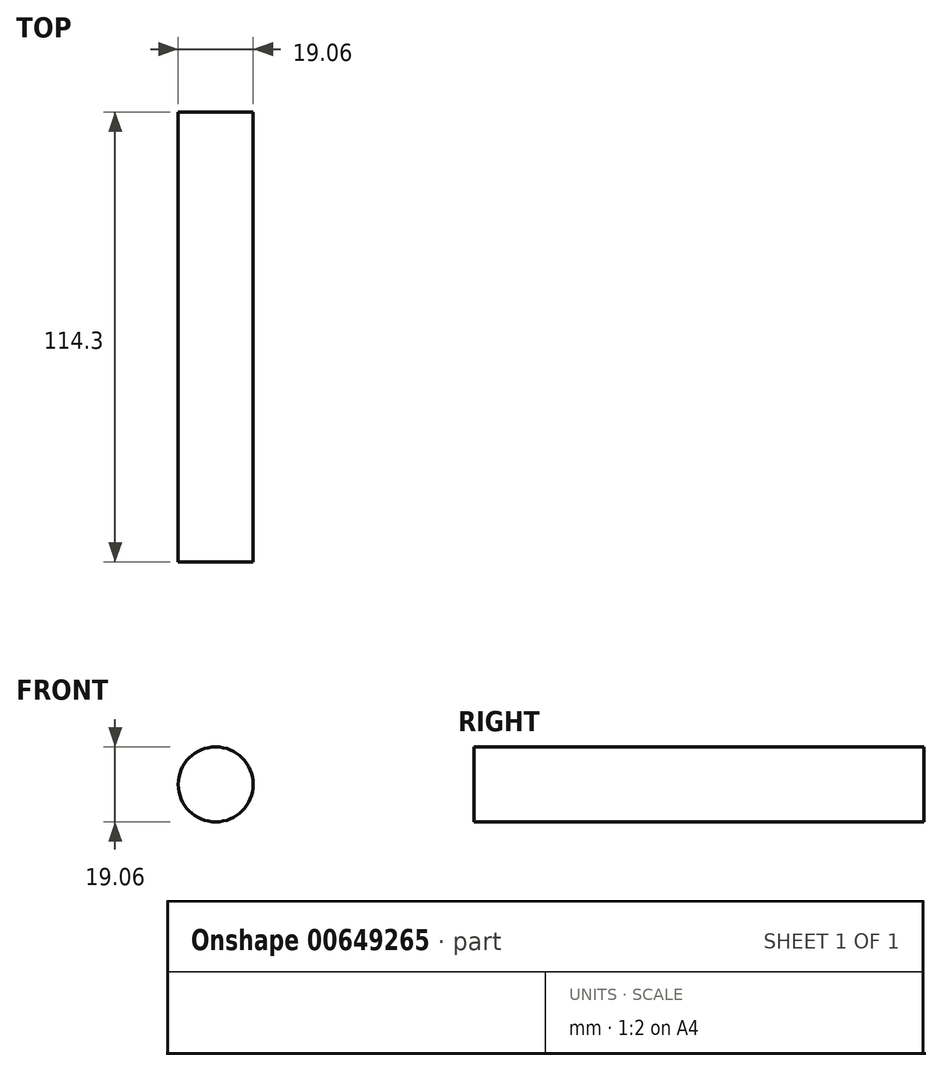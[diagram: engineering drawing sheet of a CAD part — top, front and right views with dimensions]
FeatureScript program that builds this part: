
annotation { "Feature Type Name" : "Feature", "Feature Type Description" : "" }
export const myFeature = defineFeature(function(context is Context, id is Id, definition is map)
    precondition{}
    {
        {
            var Q0;
            Q0=qCreatedBy(makeId("Front.planeOp"),FACE);
            var sketch = newSketch(context, id + "F0", { "sketchPlane" : qUnion([Q0])});
            skCircle(sketch, "E0", {"center": v(0, 0) * mm, "radius": 9.53 * mm});
            skSolve(sketch);
        }
        {
            var Q0;
            Q0=makeQuery(id+"F0.imprint","IMPRINT",FACE,{"disambiguationData":[TD([[makeQuery(id+"F0.imprint","IMPRINT",EDGE,{"derivedFrom":sQuery(id+"F0.wireOp",EDGE,"E0")}),1.0]])]});
            extrude(context, id + "F1", {"entities" : qUnion([Q0]), "depth" : 114.3 * mm, "offsetDistance" : 25.4 * mm});
        }
    });
